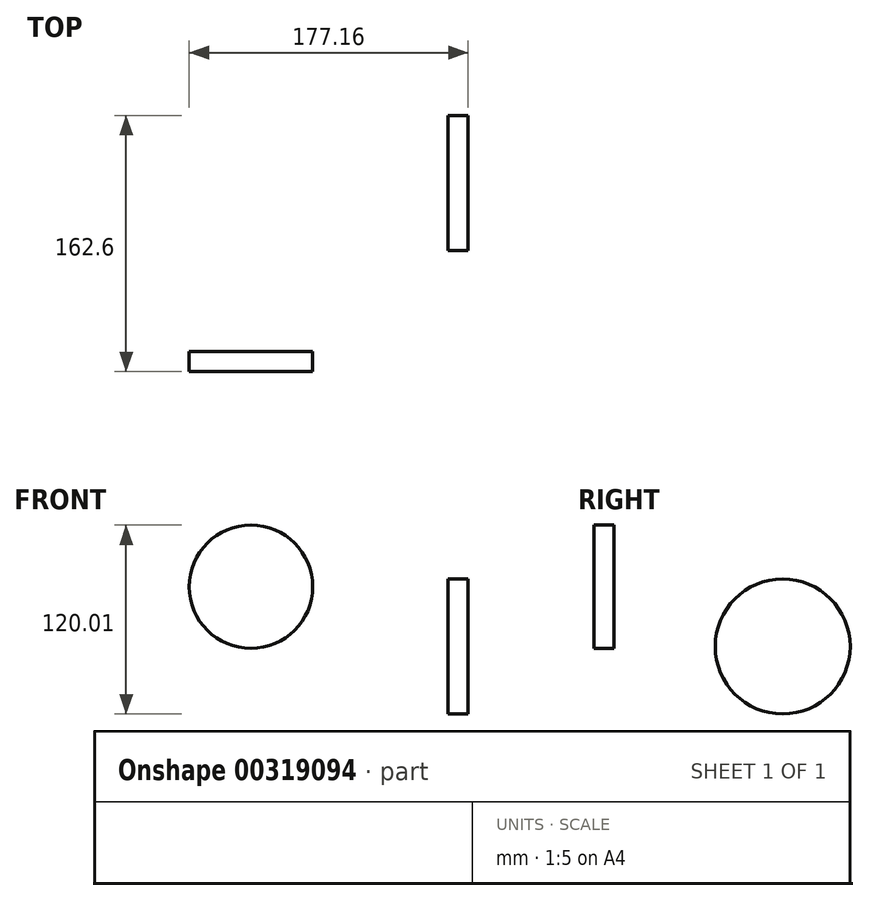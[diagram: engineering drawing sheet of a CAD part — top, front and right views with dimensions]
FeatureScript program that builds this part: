
annotation { "Feature Type Name" : "Feature", "Feature Type Description" : "" }
export const myFeature = defineFeature(function(context is Context, id is Id, definition is map)
    precondition{}
    {
        {
            var Q0;
            Q0=qCreatedBy(makeId("Front.planeOp"),FACE);
            var sketch = newSketch(context, id + "F0", { "sketchPlane" : qUnion([Q0])});
            skCircle(sketch, "E0", {"center": v(-125.27, 54.1) * mm, "radius": 39.2 * mm});
            skSolve(sketch);
        }
        {
            var Q0;
            Q0=makeQuery(id+"F0.imprint","IMPRINT",FACE,{"disambiguationData":[TD([[makeQuery(id+"F0.imprint","IMPRINT",EDGE,{"derivedFrom":sQuery(id+"F0.wireOp",EDGE,"E0")}),1.0]])]});
            extrude(context, id + "F1", {"entities" : qUnion([Q0]), "depth" : 12.7 * mm});
        }
        {
            var Q0;
            Q0=qCreatedBy(makeId("Right.planeOp"),FACE);
            var sketch = newSketch(context, id + "F2", { "sketchPlane" : qUnion([Q0])});
            skCircle(sketch, "E1", {"center": v(107.05, 16.13) * mm, "radius": 42.85 * mm});
            skSolve(sketch);
        }
        {
            var Q0;
            Q0=makeQuery(id+"F2.imprint","IMPRINT",FACE,{"disambiguationData":[TD([[makeQuery(id+"F2.imprint","IMPRINT",EDGE,{"derivedFrom":sQuery(id+"F2.wireOp",EDGE,"E1")}),1.0]])]});
            extrude(context, id + "F3", {"entities" : qUnion([Q0]), "depth" : 12.7 * mm});
        }
    });
